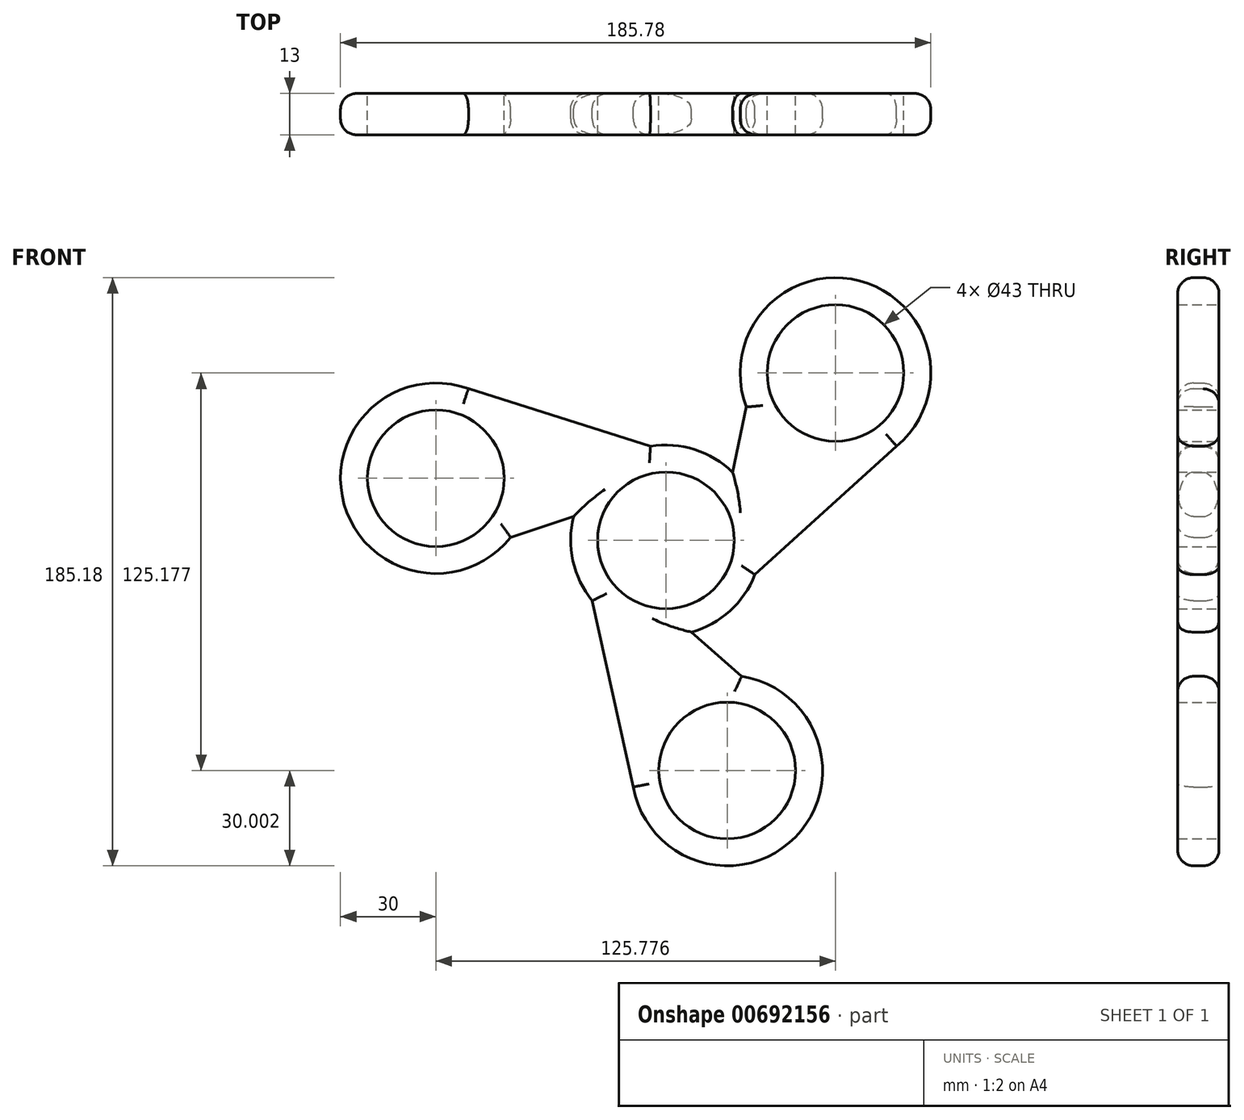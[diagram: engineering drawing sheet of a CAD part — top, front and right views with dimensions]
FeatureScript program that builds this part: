
annotation { "Feature Type Name" : "Feature", "Feature Type Description" : "" }
export const myFeature = defineFeature(function(context is Context, id is Id, definition is map)
    precondition{}
    {
        {
            var Q0;
            Q0=qCreatedBy(makeId("Front.planeOp"),FACE);
            var sketch = newSketch(context, id + "F0", { "sketchPlane" : qUnion([Q0])});
            skCircle(sketch, "E0", {"center": v(0, 0) * mm, "radius": 30 * mm});
            skCircle(sketch, "E1.MirrorC", {"center": v(53.37, 52.7) * mm, "radius": 30 * mm});
            skCircle(sketch, "E2", {"center": v(-72.41, 19.54) * mm, "radius": 30 * mm});
            skCircle(sketch, "E3", {"center": v(19.28, -72.48) * mm, "radius": 30 * mm});
            skCircle(sketch, "E4", {"center": v(-72.41, 19.54) * mm, "radius": 21.5 * mm});
            skCircle(sketch, "E5", {"center": v(53.37, 52.7) * mm, "radius": 21.5 * mm});
            skCircle(sketch, "E6", {"center": v(19.28, -72.48) * mm, "radius": 21.5 * mm});
            skLineSegment(sketch, "E7", {"start": v(-9.7, -80.2) * mm, "end": v(-29.05, 7.48) * mm});
            skLineSegment(sketch, "E8", {"start": v(-80.23, -9.43) * mm, "end": v(-29.05, 7.48) * mm});
            skLineSegment(sketch, "E9", {"start": v(74.44, 31.35) * mm, "end": v(8.04, -28.9) * mm});
            skLineSegment(sketch, "E10", {"start": v(8.04, -28.9) * mm, "end": v(48.16, -64.33) * mm});
            skLineSegment(sketch, "E11", {"start": v(-64.6, 48.5) * mm, "end": v(21, 21.42) * mm});
            skLineSegment(sketch, "E12", {"start": v(21, 21.42) * mm, "end": v(32.02, 73.78) * mm});
            skCircle(sketch, "E13.cCircle", {"center": v(0, 0) * mm, "radius": 15 * mm, "construction": true});
            skLineSegment(sketch, "E13.0", {"start": v(8.04, -28.9) * mm, "end": v(-29.05, 7.48) * mm});
            skLineSegment(sketch, "E13.1", {"start": v(-29.05, 7.48) * mm, "end": v(21, 21.42) * mm});
            skLineSegment(sketch, "E13.2", {"start": v(21, 21.42) * mm, "end": v(8.04, -28.9) * mm});
            skPoint(sketch, "E13.0.midPoint", {"position": v(-10.5, -10.7) * mm});
            skCircle(sketch, "E14", {"center": v(0, 0) * mm, "radius": 21.5 * mm});
            skSolve(sketch);
        }
        {
            var Q0;
            Q0 = qSketchRegion(id + "F0", true);
            extrude(context, id + "F1", {"entities" : qUnion([Q0]), "depth" : 13 * mm, "offsetDistance" : 25 * mm});
        }
        {
            var Q0;
            Q0=makeQuery(id+"F1.opExtrude","CAP_EDGE",EDGE,{"disambiguationData":[OSD([sQuery(id+"F0.wireOp",EDGE,"E1.MirrorC")])],"isStart":true});
            var Q1;
            Q1=makeQuery(id+"F1.opExtrude","CAP_EDGE",EDGE,{"disambiguationData":[OSD([sQuery(id+"F0.wireOp",EDGE,"E12")])],"isStart":true});
            var Q2;
            {var subQ0=sQuery(id+"F0.wireOp",EDGE,"E9");var subQ1=sQuery(id+"F0.wireOp",EDGE,"E0");Q2=makeQuery(id+"F1.opExtrude","CAP_EDGE",EDGE,{"disambiguationData":[OSD([subQ1]),TDD([makeQuery(id+"F0.imprint","IMPRINT",EDGE,{"disambiguationData":[TD([[makeQuery(id+"F0.imprint","INTERSECT",VERTEX,{"derivedFrom":[subQ1,subQ0]}),1.0]])],"derivedFrom":subQ1})])],"isStart":true});}
            var Q3;
            Q3=makeQuery(id+"F1.opExtrude","CAP_EDGE",EDGE,{"disambiguationData":[OSD([sQuery(id+"F0.wireOp",EDGE,"E10")])],"isStart":true});
            var Q4;
            Q4=makeQuery(id+"F1.opExtrude","CAP_EDGE",EDGE,{"disambiguationData":[OSD([sQuery(id+"F0.wireOp",EDGE,"E3")])],"isStart":true});
            var Q5;
            {var subQ0=sQuery(id+"F0.wireOp",EDGE,"E7");var subQ1=sQuery(id+"F0.wireOp",EDGE,"E0");Q5=makeQuery(id+"F1.opExtrude","CAP_EDGE",EDGE,{"disambiguationData":[OSD([subQ1]),TDD([makeQuery(id+"F0.imprint","IMPRINT",EDGE,{"disambiguationData":[TD([[makeQuery(id+"F0.imprint","INTERSECT",VERTEX,{"derivedFrom":[subQ1,subQ0]}),1.0]])],"derivedFrom":subQ1})])],"isStart":true});}
            var Q6;
            Q6=makeQuery(id+"F1.opExtrude","CAP_EDGE",EDGE,{"disambiguationData":[OSD([sQuery(id+"F0.wireOp",EDGE,"E2")])],"isStart":true});
            var Q7;
            Q7=makeQuery(id+"F1.opExtrude","CAP_EDGE",EDGE,{"disambiguationData":[OSD([sQuery(id+"F0.wireOp",EDGE,"E8")])],"isStart":true});
            var Q8;
            {var subQ0=sQuery(id+"F0.wireOp",EDGE,"E11");var subQ1=sQuery(id+"F0.wireOp",EDGE,"E0");Q8=makeQuery(id+"F1.opExtrude","CAP_EDGE",EDGE,{"disambiguationData":[OSD([subQ1]),TDD([makeQuery(id+"F0.imprint","IMPRINT",EDGE,{"disambiguationData":[TD([[makeQuery(id+"F0.imprint","INTERSECT",VERTEX,{"derivedFrom":[subQ1,subQ0]}),1.0]])],"derivedFrom":subQ1})])],"isStart":true});}
            var Q9;
            Q9=makeQuery(id+"F1.opExtrude","CAP_EDGE",EDGE,{"disambiguationData":[OSD([sQuery(id+"F0.wireOp",EDGE,"E3")])],"isStart":false});
            var Q10;
            Q10=makeQuery(id+"F1.opExtrude","CAP_EDGE",EDGE,{"disambiguationData":[OSD([sQuery(id+"F0.wireOp",EDGE,"E7")])],"isStart":false});
            var Q11;
            Q11=makeQuery(id+"F1.opExtrude","CAP_EDGE",EDGE,{"disambiguationData":[OSD([sQuery(id+"F0.wireOp",EDGE,"E10")])],"isStart":false});
            var Q12;
            {var subQ0=sQuery(id+"F0.wireOp",EDGE,"E9");var subQ1=sQuery(id+"F0.wireOp",EDGE,"E0");Q12=makeQuery(id+"F1.opExtrude","CAP_EDGE",EDGE,{"disambiguationData":[OSD([subQ1]),TDD([makeQuery(id+"F0.imprint","IMPRINT",EDGE,{"disambiguationData":[TD([[makeQuery(id+"F0.imprint","INTERSECT",VERTEX,{"derivedFrom":[subQ1,subQ0]}),1.0]])],"derivedFrom":subQ1})])],"isStart":false});}
            var Q13;
            Q13=makeQuery(id+"F1.opExtrude","CAP_EDGE",EDGE,{"disambiguationData":[OSD([sQuery(id+"F0.wireOp",EDGE,"E9")])],"isStart":false});
            var Q14;
            Q14=makeQuery(id+"F1.opExtrude","CAP_EDGE",EDGE,{"disambiguationData":[OSD([sQuery(id+"F0.wireOp",EDGE,"E1.MirrorC")])],"isStart":false});
            var Q15;
            Q15=makeQuery(id+"F1.opExtrude","CAP_EDGE",EDGE,{"disambiguationData":[OSD([sQuery(id+"F0.wireOp",EDGE,"E12")])],"isStart":false});
            var Q16;
            {var subQ0=sQuery(id+"F0.wireOp",EDGE,"E11");var subQ1=sQuery(id+"F0.wireOp",EDGE,"E0");Q16=makeQuery(id+"F1.opExtrude","CAP_EDGE",EDGE,{"disambiguationData":[OSD([subQ1]),TDD([makeQuery(id+"F0.imprint","IMPRINT",EDGE,{"disambiguationData":[TD([[makeQuery(id+"F0.imprint","INTERSECT",VERTEX,{"derivedFrom":[subQ1,subQ0]}),1.0]])],"derivedFrom":subQ1})])],"isStart":false});}
            var Q17;
            Q17=makeQuery(id+"F1.opExtrude","CAP_EDGE",EDGE,{"disambiguationData":[OSD([sQuery(id+"F0.wireOp",EDGE,"E11")])],"isStart":false});
            var Q18;
            Q18=makeQuery(id+"F1.opExtrude","CAP_EDGE",EDGE,{"disambiguationData":[OSD([sQuery(id+"F0.wireOp",EDGE,"E2")])],"isStart":false});
            var Q19;
            Q19=makeQuery(id+"F1.opExtrude","CAP_EDGE",EDGE,{"disambiguationData":[OSD([sQuery(id+"F0.wireOp",EDGE,"E8")])],"isStart":false});
            var Q20;
            {var subQ0=sQuery(id+"F0.wireOp",EDGE,"E7");var subQ1=sQuery(id+"F0.wireOp",EDGE,"E0");Q20=makeQuery(id+"F1.opExtrude","CAP_EDGE",EDGE,{"disambiguationData":[OSD([subQ1]),TDD([makeQuery(id+"F0.imprint","IMPRINT",EDGE,{"disambiguationData":[TD([[makeQuery(id+"F0.imprint","INTERSECT",VERTEX,{"derivedFrom":[subQ1,subQ0]}),1.0]])],"derivedFrom":subQ1})])],"isStart":false});}
            fillet(context, id + "F2", {"entities" : qUnion([Q0, Q1, Q2, Q3, Q4, Q5, Q6, Q7, Q8, Q9, Q10, Q11, Q12, Q13, Q14, Q15, Q16, Q17, Q18, Q19, Q20]), "radius" : 5 * mm, "tangentPropagation" : true, "allowEdgeOverflow" : false});
        }
    });
